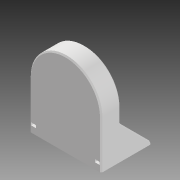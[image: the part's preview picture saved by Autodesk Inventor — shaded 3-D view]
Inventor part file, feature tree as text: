
AUTODESK INVENTOR PART (.ipt)
format: ipt  version: 2020 (Build 240168000, 168)  size: 419,840 bytes
history: native  units: mm
features: extrude x9, sketch x9, projected_geometry x2, mirror x1, plane x1, chamfer x1, fillet x1, revolve x1
ambient origin geometry x8: Origin, YZ Plane, XZ Plane, XY Plane, X Axis, Y Axis, Z Axis, Center Point
bodies: Solid1 (feature_tree)
feature tree (25):
  extrude  "Extrusion1"  Depth=80.0mm
  extrude  "Extrusion2"  Depth=2.0mm
  extrude  "Extrusion3"  Depth=1.0mm
  extrude  "Extrusion7"  Depth=50.0mm TaperAngle=360.0deg
  mirror  "Mirror1"
  extrude  "Extrusion4"  Depth=5.5mm
  plane  "Work Plane1"
  sketch  "Sketch6"  dims[d14=0.0mm d15=0.0mm d16=5.5mm]
  extrude  "Extrusion5"  Depth=6.5mm
  extrude  "Extrusion6"  Depth=18.0mm TaperAngle=0.0deg
  chamfer  "Chamfer1"  Distance=4.5mm
  fillet  "Fillet2"  Radius=20.75mm
  revolve  "Revolution1"  Angle=45.0deg
  extrude  "Extrusion8"  Depth=50.0mm
  extrude  "Extrusion9"  Depth=5.0mm
  sketch  "Sketch1"  dims[d0=95.05mm d2=80.0mm]
  sketch  "Sketch2"  dims[d3=32.5mm d4=0.0mm d5=2.0mm]
  sketch  "Sketch3"  dims[d6=1.0mm d7=0.0mm d8=5.2mm]
  sketch  "Sketch5"  dims[d9=55.0mm d10=50.0mm d12=360.0deg]
  sketch  "Sketch7"  dims[d17=6.5mm d18=6.5mm]
  projected_geometry  "Projected Loop2"
  sketch  "Sketch10"  dims[d19=6.5mm d20=18.0mm d21=0.0mm]
  projected_geometry  "Projected Loop4"
  sketch  "Sketch11"  dims[d22=-15.0mm]
  sketch  "Sketch12"  dims[d23=8.2mm d24=4.5mm d25=0.0mm d26=20.75mm d27=0.0mm d29=2.0mm d30=2.0mm d31=45.0deg d32=50.0mm d33=5.0mm d34=135.0deg d35=15.0mm d36=0.0mm d37=10.0mm d38=5.0mm d43=60.0mm d44=11.1mm d45=1.0mm d46=0.5mm d47=2.0mm d48=2.5mm d49=7.0mm d51=2.0mm d52=120.0deg d53=2.0mm d54=11.1mm d55=2.5mm d56=120.0deg d57=90.0deg d58=55.0mm d59=75.0mm d60=10.0mm d61=0.0mm d62=10.0mm d63=0.0mm]
